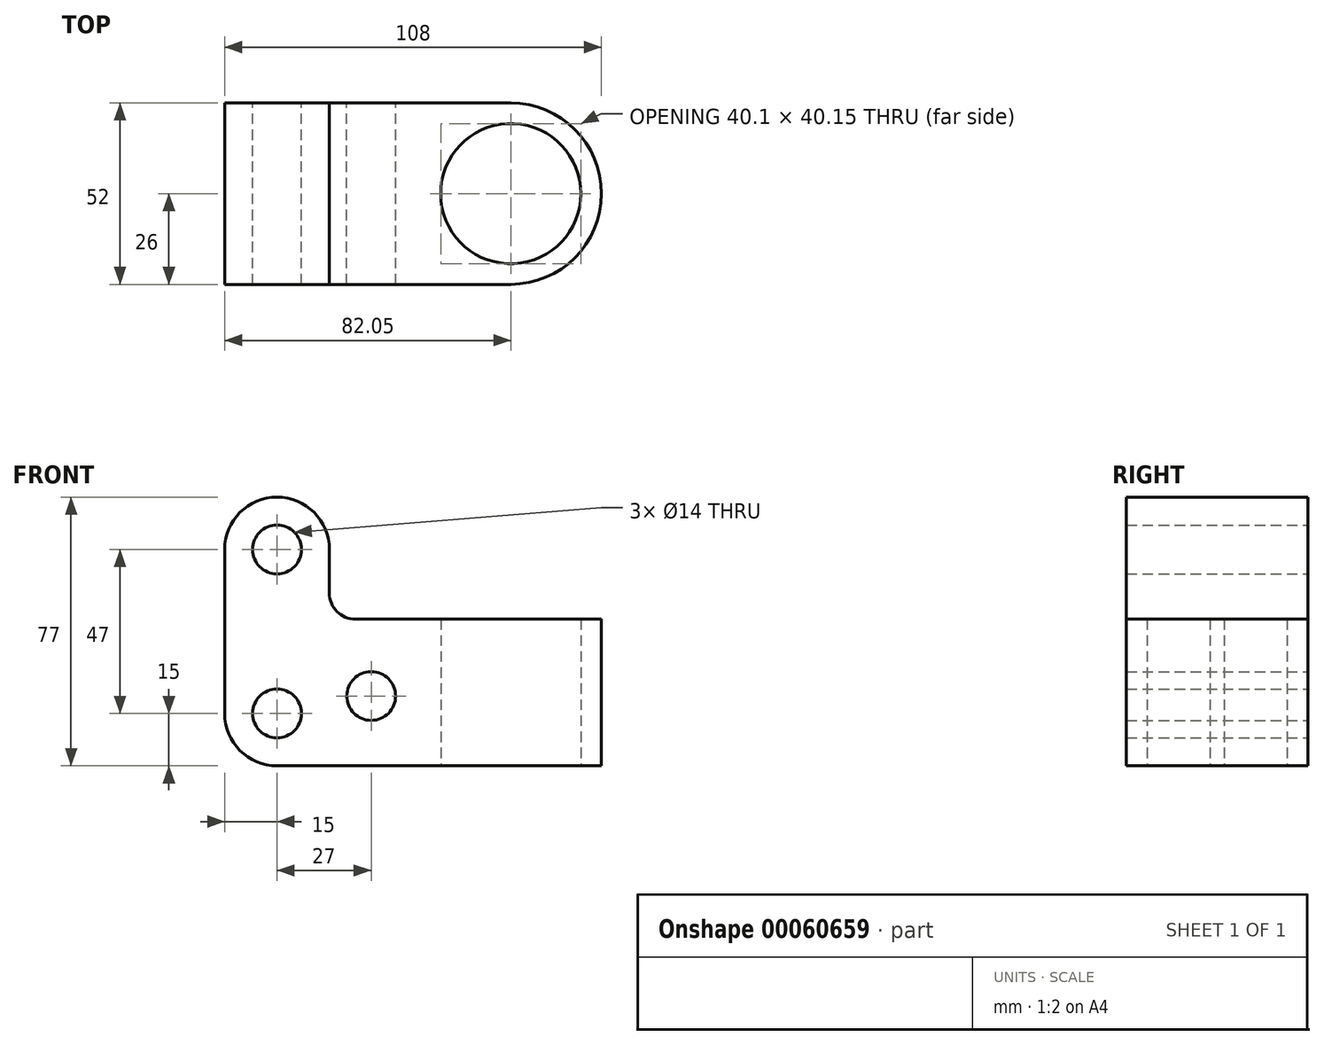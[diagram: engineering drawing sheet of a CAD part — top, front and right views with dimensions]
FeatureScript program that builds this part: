
annotation { "Feature Type Name" : "Feature", "Feature Type Description" : "" }
export const myFeature = defineFeature(function(context is Context, id is Id, definition is map)
    precondition{}
    {
        {
            var Q0;
            Q0=qCreatedBy(makeId("Front.planeOp"),FACE);
            var sketch = newSketch(context, id + "F0", { "sketchPlane" : qUnion([Q0])});
            skLineSegment(sketch, "E0", {"start": v(0, 0) * mm, "end": v(-47, 0) * mm});
            skLineSegment(sketch, "E1", {"start": v(-32, 62) * mm, "end": v(-32, 49.5) * mm});
            skLineSegment(sketch, "E2", {"start": v(-24.5, 42) * mm, "end": v(0, 42) * mm});
            skLineSegment(sketch, "E3", {"start": v(0, 42) * mm, "end": v(0, 0) * mm});
            skArc(sketch, "E4", {"start": v(-32, 62) * mm, "mid": v(-47, 77) * mm, "end": v(-62, 62) * mm});
            skLineSegment(sketch, "E5", {"start": v(-62, 15) * mm, "end": v(-62, 62) * mm});
            skArc(sketch, "E6", {"start": v(-62, 15) * mm, "mid": v(-57.6, 4.4) * mm, "end": v(-47, 0) * mm});
            skCircle(sketch, "E7", {"center": v(-47, 62) * mm, "radius": 7 * mm});
            skCircle(sketch, "E8", {"center": v(-47, 15) * mm, "radius": 7 * mm});
            skCircle(sketch, "E9", {"center": v(-20, 20) * mm, "radius": 7 * mm});
            skArc(sketch, "E10", {"start": v(-32, 49.5) * mm, "mid": v(-29.8, 44.2) * mm, "end": v(-24.5, 42) * mm});
            skSolve(sketch);
        }
        {
            var Q0;
            Q0=makeQuery(id+"F0.imprint","IMPRINT",FACE,{"disambiguationData":[TD([[makeQuery(id+"F0.imprint","IMPRINT",EDGE,{"derivedFrom":sQuery(id+"F0.wireOp",EDGE,"E0")}),-1.0]])]});
            extrude(context, id + "F1", {"entities" : qUnion([Q0]), "depth" : 52 * mm});
        }
        {
            var Q0;
            Q0=qCreatedBy(makeId("Top.planeOp"),FACE);
            var sketch = newSketch(context, id + "F2", { "sketchPlane" : qUnion([Q0])});
            skLineSegment(sketch, "E11.bottom", {"start": v(0, 0) * mm, "end": v(20, 0) * mm});
            skLineSegment(sketch, "E11.top", {"start": v(0, -52) * mm, "end": v(20, -52) * mm});
            skLineSegment(sketch, "E11.left", {"start": v(0, 0) * mm, "end": v(0, -52) * mm});
            skCircle(sketch, "E12", {"center": v(20, -26) * mm, "radius": 20.1 * mm});
            skArc(sketch, "E13.trimOffspring", {"start": v(20, -52) * mm, "mid": v(46, -26) * mm, "end": v(20, 0) * mm});
            skSolve(sketch);
        }
        {
            var Q0;
            {var subQ0=sQuery(id+"F2.wireOp",EDGE,"E12");var subQ1=sQuery(id+"F2.wireOp",EDGE,"E11.left");var subQ2=makeQuery(id+"F2.imprint","INTERSECT",VERTEX,{"disambiguationData":[OD(0.0)],"derivedFrom":[subQ1,subQ0]});Q0=makeQuery(id+"F2.imprint","IMPRINT",FACE,{"disambiguationData":[TD([[makeQuery(id+"F2.imprint","IMPRINT",EDGE,{"disambiguationData":[TD([[subQ2,-1.0]])],"derivedFrom":subQ1}),-1.0]])]});}
            var Q1;
            {var subQ4=sQuery(id+"F2.wireOp",EDGE,"E11.bottom");Q1=makeQuery(id+"F2.imprint","IMPRINT",FACE,{"disambiguationData":[TD([[makeQuery(id+"F2.imprint","IMPRINT",EDGE,{"derivedFrom":subQ4}),-1.0]])]});}
            extrude(context, id + "F3", {"entities" : qUnion([Q0, Q1]), "operationType" : NewBodyOperationType.ADD, "depth" : 42 * mm});
        }
    });
